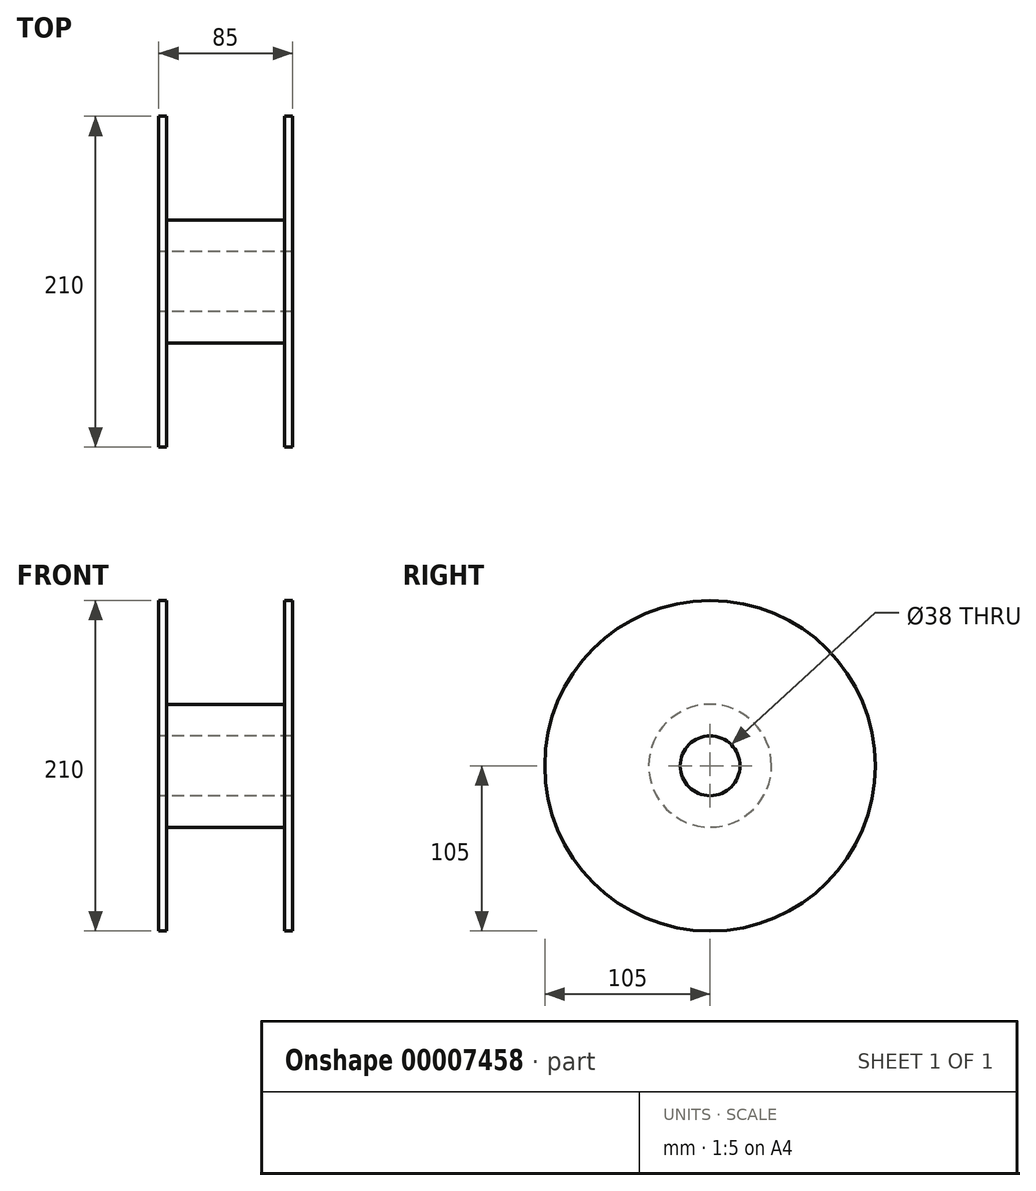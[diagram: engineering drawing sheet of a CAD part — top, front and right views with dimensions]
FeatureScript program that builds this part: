
annotation { "Feature Type Name" : "Feature", "Feature Type Description" : "" }
export const myFeature = defineFeature(function(context is Context, id is Id, definition is map)
    precondition{}
    {
        {
            var Q0;
            Q0=qCreatedBy(makeId("Top.planeOp"),FACE);
            var sketch = newSketch(context, id + "F0", { "sketchPlane" : qUnion([Q0])});
            skLineSegment(sketch, "E0", {"start": v(0, 0) * mm, "end": v(0, 19) * mm});
            skLineSegment(sketch, "E1", {"start": v(0, 19) * mm, "end": v(85, 19) * mm});
            skLineSegment(sketch, "E2", {"start": v(85, 19) * mm, "end": v(85, 105) * mm});
            skLineSegment(sketch, "E3", {"start": v(85, 105) * mm, "end": v(80, 105) * mm});
            skLineSegment(sketch, "E4", {"start": v(80, 105) * mm, "end": v(80, 39) * mm});
            skLineSegment(sketch, "E5", {"start": v(80, 39) * mm, "end": v(5, 39) * mm});
            skLineSegment(sketch, "E6", {"start": v(5, 39) * mm, "end": v(5, 105) * mm});
            skLineSegment(sketch, "E7", {"start": v(5, 105) * mm, "end": v(0, 105) * mm});
            skLineSegment(sketch, "E8", {"start": v(0, 105) * mm, "end": v(0, 19) * mm});
            skLineSegment(sketch, "E9", {"start": v(0, 0) * mm, "end": v(153.9, 0) * mm, "construction": true});
            skSolve(sketch);
        }
        {
            var Q0;
            Q0=makeQuery(id+"F0.imprint","IMPRINT",FACE,{"disambiguationData":[TD([[makeQuery(id+"F0.imprint","IMPRINT",EDGE,{"derivedFrom":sQuery(id+"F0.wireOp",EDGE,"E1")}),1.0]])]});
            var Q1;
            Q1=sQuery(id+"F0.wireOp",EDGE,"E9");
            revolve(context, id + "F1", {"entities" : qUnion([Q0]), "axis" : qUnion([Q1]), "revolveType" : RevolveType.FULL});
        }
    });
